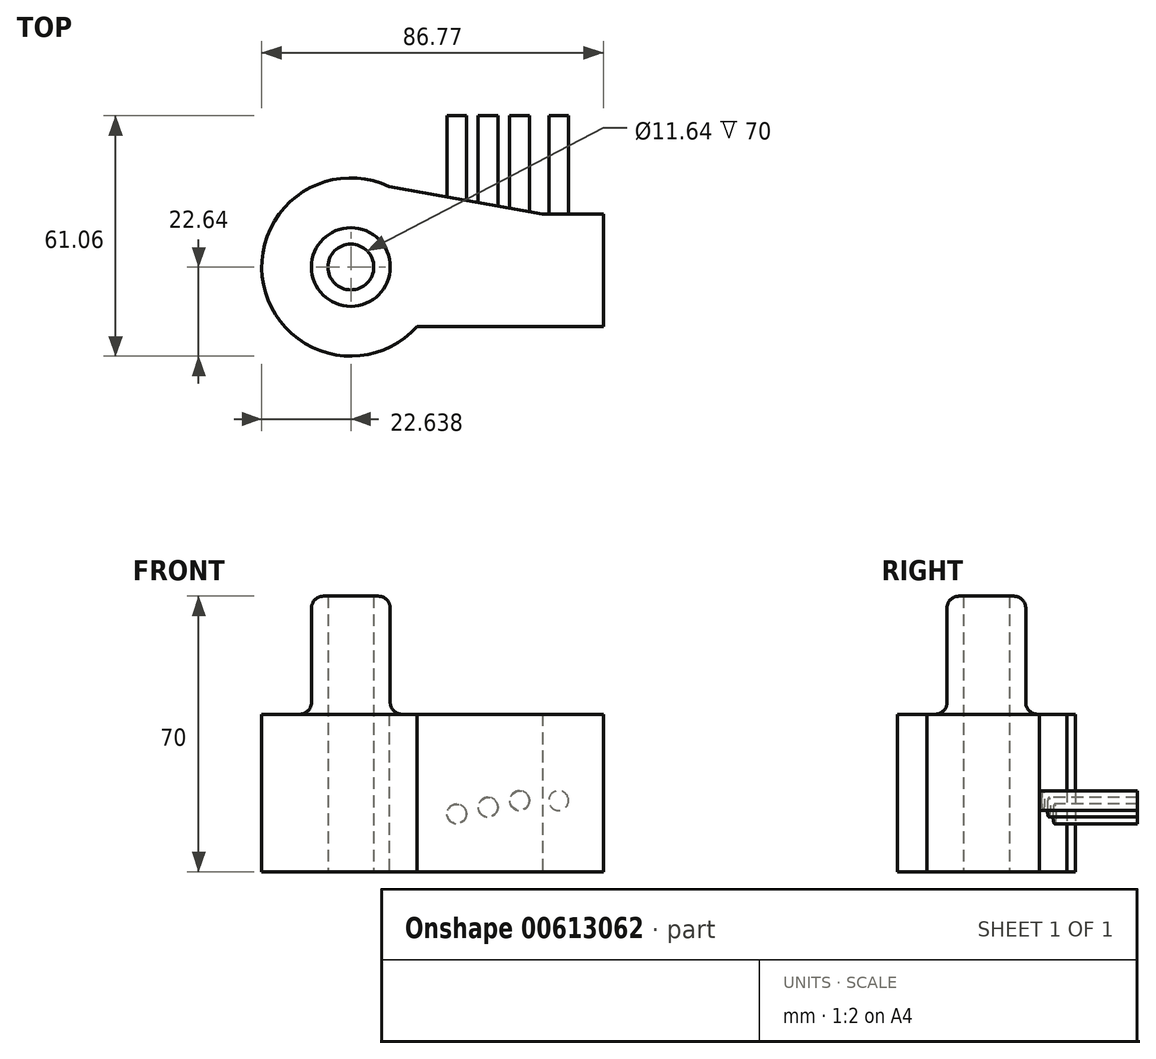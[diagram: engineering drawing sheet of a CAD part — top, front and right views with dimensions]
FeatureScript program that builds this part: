
annotation { "Feature Type Name" : "Feature", "Feature Type Description" : "" }
export const myFeature = defineFeature(function(context is Context, id is Id, definition is map)
    precondition{}
    {
        {
            var Q0;
            Q0=qCreatedBy(makeId("Top.planeOp"),FACE);
            var sketch = newSketch(context, id + "F0", { "sketchPlane" : qUnion([Q0])});
            skLineSegment(sketch, "E0.bottom", {"start": v(-26.9, 13.42) * mm, "end": v(37.23, 13.42) * mm});
            skLineSegment(sketch, "E0.top", {"start": v(-26.9, -15.12) * mm, "end": v(37.23, -15.12) * mm});
            skLineSegment(sketch, "E0.left", {"start": v(-26.9, 13.42) * mm, "end": v(-26.9, -15.12) * mm});
            skLineSegment(sketch, "E0.right", {"start": v(37.23, 13.42) * mm, "end": v(37.23, -15.12) * mm});
            skCircle(sketch, "E1", {"center": v(-26.9, 0) * mm, "radius": 22.64 * mm});
            skCircle(sketch, "E2", {"center": v(-26.9, 0) * mm, "radius": 10 * mm});
            skLineSegment(sketch, "E3", {"start": v(-17.2, 20.46) * mm, "end": v(21.8, 13.42) * mm});
            skCircle(sketch, "E4", {"center": v(-26.9, 0) * mm, "radius": 5.82 * mm});
            skSolve(sketch);
        }
        {
            var Q0;
            {var subQ0=sQuery(id+"F0.wireOp",EDGE,"E2");var subQ1=sQuery(id+"F0.wireOp",EDGE,"E0.left");var subQ2=makeQuery(id+"F0.imprint","INTERSECT",VERTEX,{"disambiguationData":[OD(0.0)],"derivedFrom":[subQ1,subQ0]});Q0=makeQuery(id+"F0.imprint","IMPRINT",FACE,{"disambiguationData":[TD([[makeQuery(id+"F0.imprint","IMPRINT",EDGE,{"disambiguationData":[TD([[subQ2,-1.0]])],"derivedFrom":subQ1}),1.0]])]});}
            var Q1;
            {var subQ0=sQuery(id+"F0.wireOp",EDGE,"E2");var subQ1=sQuery(id+"F0.wireOp",EDGE,"E0.left");var subQ2=makeQuery(id+"F0.imprint","INTERSECT",VERTEX,{"disambiguationData":[OD(0.0)],"derivedFrom":[subQ1,subQ0]});Q1=makeQuery(id+"F0.imprint","IMPRINT",FACE,{"disambiguationData":[TD([[makeQuery(id+"F0.imprint","IMPRINT",EDGE,{"disambiguationData":[TD([[subQ2,-1.0]])],"derivedFrom":subQ1}),-1.0]])]});}
            extrude(context, id + "F1", {"entities" : qUnion([Q0, Q1]), "depth" : 70 * mm, "offsetDistance" : 25 * mm});
        }
        {
            var Q0;
            Q0 = qSketchRegion(id + "F0", true);
            extrude(context, id + "F2", {"entities" : qUnion([Q0]), "operationType" : NewBodyOperationType.ADD, "depth" : 40 * mm, "offsetDistance" : 25 * mm});
        }
        {
            var Q0;
            Q0=makeQuery(id+"F2.opExtrude","CAP_EDGE",EDGE,{"disambiguationData":[OSD([sQuery(id+"F0.wireOp",EDGE,"E2")])],"isStart":false});
            var Q1;
            Q1=makeQuery(id+"F1.opExtrude","SWEPT_FACE",FACE,{"disambiguationData":[OSD([sQuery(id+"F0.wireOp",EDGE,"E2")])]});
            fillet(context, id + "F3", {"entities" : qUnion([Q0, Q1]), "radius" : 3 * mm, "tangentPropagation" : true, "allowEdgeOverflow" : false});
        }
        {
            var Q0;
            Q0=makeQuery(id+"F2.opExtrude","SWEPT_FACE",FACE,{"disambiguationData":[OSD([sQuery(id+"F0.wireOp",EDGE,"E0.bottom")])]});
            var sketch = newSketch(context, id + "F4", { "sketchPlane" : qUnion([Q0])});
            skCircle(sketch, "E5", {"center": v(0, 14.67) * mm, "radius": 2.5 * mm});
            skCircle(sketch, "E6", {"center": v(-7.96, 16.4) * mm, "radius": 2.5 * mm});
            skCircle(sketch, "E7", {"center": v(-15.96, 18.07) * mm, "radius": 2.5 * mm});
            skCircle(sketch, "E8", {"center": v(-25.88, 18.07) * mm, "radius": 2.5 * mm});
            skSolve(sketch);
        }
        {
            var Q0;
            Q0=makeQuery(id+"F4.imprint","IMPRINT",FACE,{"disambiguationData":[TD([[makeQuery(id+"F4.imprint","IMPRINT",EDGE,{"derivedFrom":sQuery(id+"F4.wireOp",EDGE,"E8")}),1.0]])]});
            var Q1;
            Q1=makeQuery(id+"F4.imprint","IMPRINT",FACE,{"disambiguationData":[TD([[makeQuery(id+"F4.imprint","IMPRINT",EDGE,{"derivedFrom":sQuery(id+"F4.wireOp",EDGE,"E7")}),1.0]])]});
            var Q2;
            Q2=makeQuery(id+"F4.imprint","IMPRINT",FACE,{"disambiguationData":[TD([[makeQuery(id+"F4.imprint","IMPRINT",EDGE,{"derivedFrom":sQuery(id+"F4.wireOp",EDGE,"E6")}),1.0]])]});
            var Q3;
            Q3=makeQuery(id+"F4.imprint","IMPRINT",FACE,{"disambiguationData":[TD([[makeQuery(id+"F4.imprint","IMPRINT",EDGE,{"derivedFrom":sQuery(id+"F4.wireOp",EDGE,"E5")}),1.0]])]});
            extrude(context, id + "F5", {"entities" : qUnion([Q0, Q1, Q2, Q3]), "operationType" : NewBodyOperationType.ADD, "depth" : 25 * mm, "offsetDistance" : 25 * mm});
        }
    });
